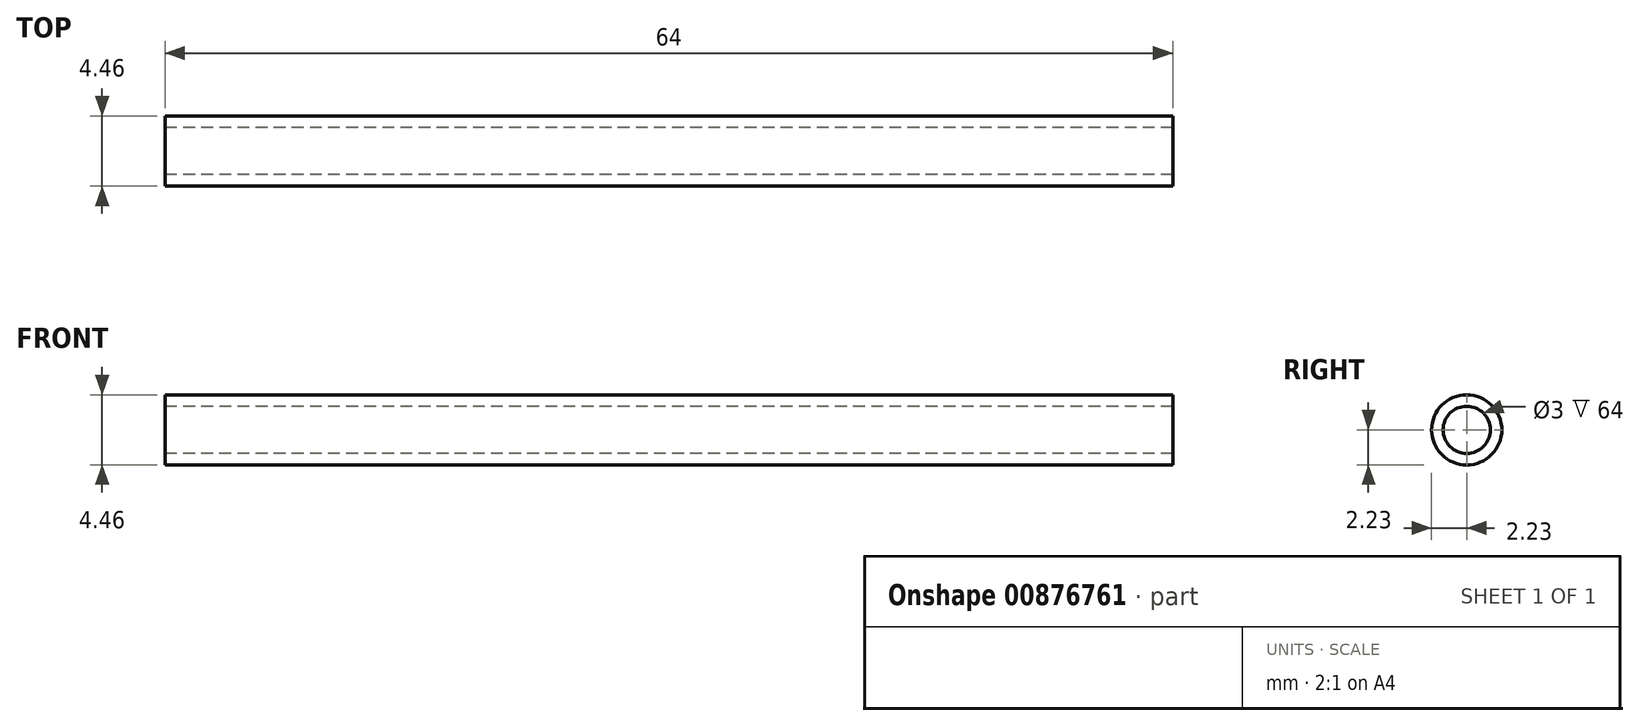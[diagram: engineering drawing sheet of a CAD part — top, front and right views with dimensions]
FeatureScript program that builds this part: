
annotation { "Feature Type Name" : "Feature", "Feature Type Description" : "" }
export const myFeature = defineFeature(function(context is Context, id is Id, definition is map)
    precondition{}
    {
        {
            var Q0;
            Q0=qCreatedBy(makeId("Right.planeOp"),FACE);
            var sketch = newSketch(context, id + "F0", { "sketchPlane" : qUnion([Q0])});
            skCircle(sketch, "E0", {"center": v(0, 0) * mm, "radius": 1.5 * mm});
            skCircle(sketch, "E1", {"center": v(0, 0) * mm, "radius": 2.23 * mm});
            skSolve(sketch);
        }
        {
            var Q0;
            Q0=makeQuery(id+"F0.imprint","IMPRINT",FACE,{"disambiguationData":[TD([[makeQuery(id+"F0.imprint","IMPRINT",EDGE,{"derivedFrom":sQuery(id+"F0.wireOp",EDGE,"E0")}),-1.0]])]});
            extrude(context, id + "F1", {"entities" : qUnion([Q0]), "depth" : 64 * mm, "offsetDistance" : 25.4 * mm});
        }
    });
